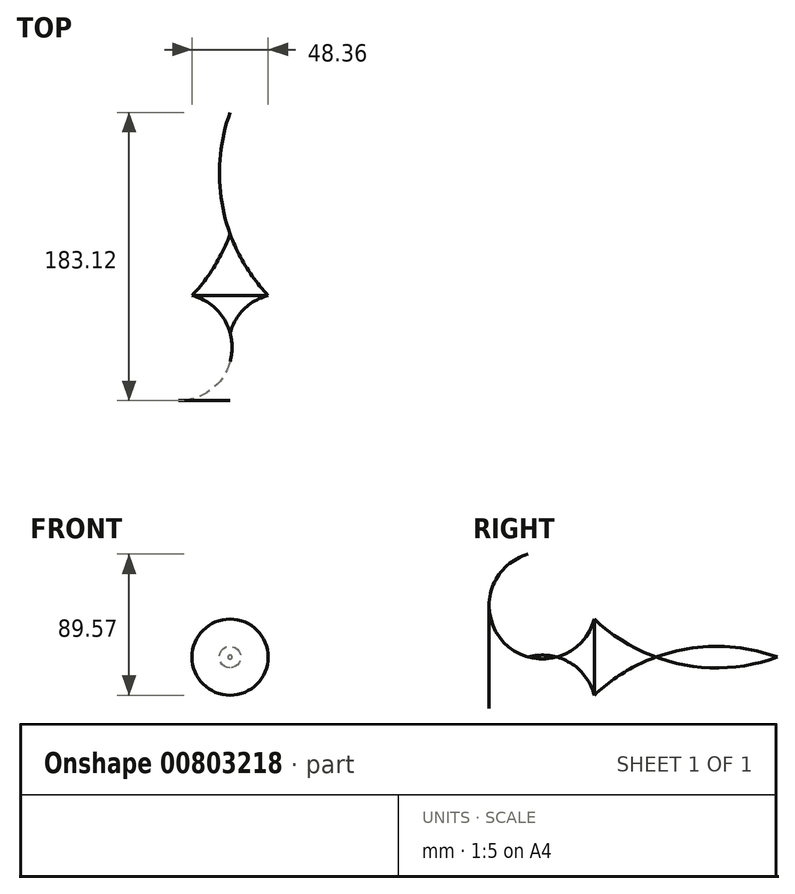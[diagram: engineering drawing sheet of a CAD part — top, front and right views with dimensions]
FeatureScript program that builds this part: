
annotation { "Feature Type Name" : "Feature", "Feature Type Description" : "" }
export const myFeature = defineFeature(function(context is Context, id is Id, definition is map)
    precondition{}
    {
        {
            var Q0;
            Q0=qCreatedBy(makeId("Top.planeOp"),FACE);
            var sketch = newSketch(context, id + "F0", { "sketchPlane" : qUnion([Q0])});
            skLineSegment(sketch, "E0", {"start": v(0, 74.64) * mm, "end": v(0, -75.37) * mm, "construction": true});
            skArc(sketch, "E1", {"start": v(24.18, 0) * mm, "mid": v(8.92, -8.63) * mm, "end": v(0, -23.72) * mm});
            skArc(sketch, "E2", {"start": v(0, 39.06) * mm, "mid": v(10.08, 18.28) * mm, "end": v(24.18, 0) * mm});
            skLineSegment(sketch, "E3", {"start": v(0, 39.06) * mm, "end": v(0, -23.72) * mm});
            skSolve(sketch);
        }
        {
            var Q0;
            Q0=makeQuery(id+"F0.imprint","IMPRINT",FACE,{"disambiguationData":[TD([[makeQuery(id+"F0.imprint","IMPRINT",EDGE,{"derivedFrom":sQuery(id+"F0.wireOp",EDGE,"E1")}),-1.0]])]});
            var Q1;
            Q1=sQuery(id+"F0.wireOp",EDGE,"E0");
            revolve(context, id + "F1", {"surfaceOperationType" : NewSurfaceOperationType.NEW, "entities" : qUnion([Q0]), "axis" : qUnion([Q1]), "revolveType" : RevolveType.FULL});
        }
    });
